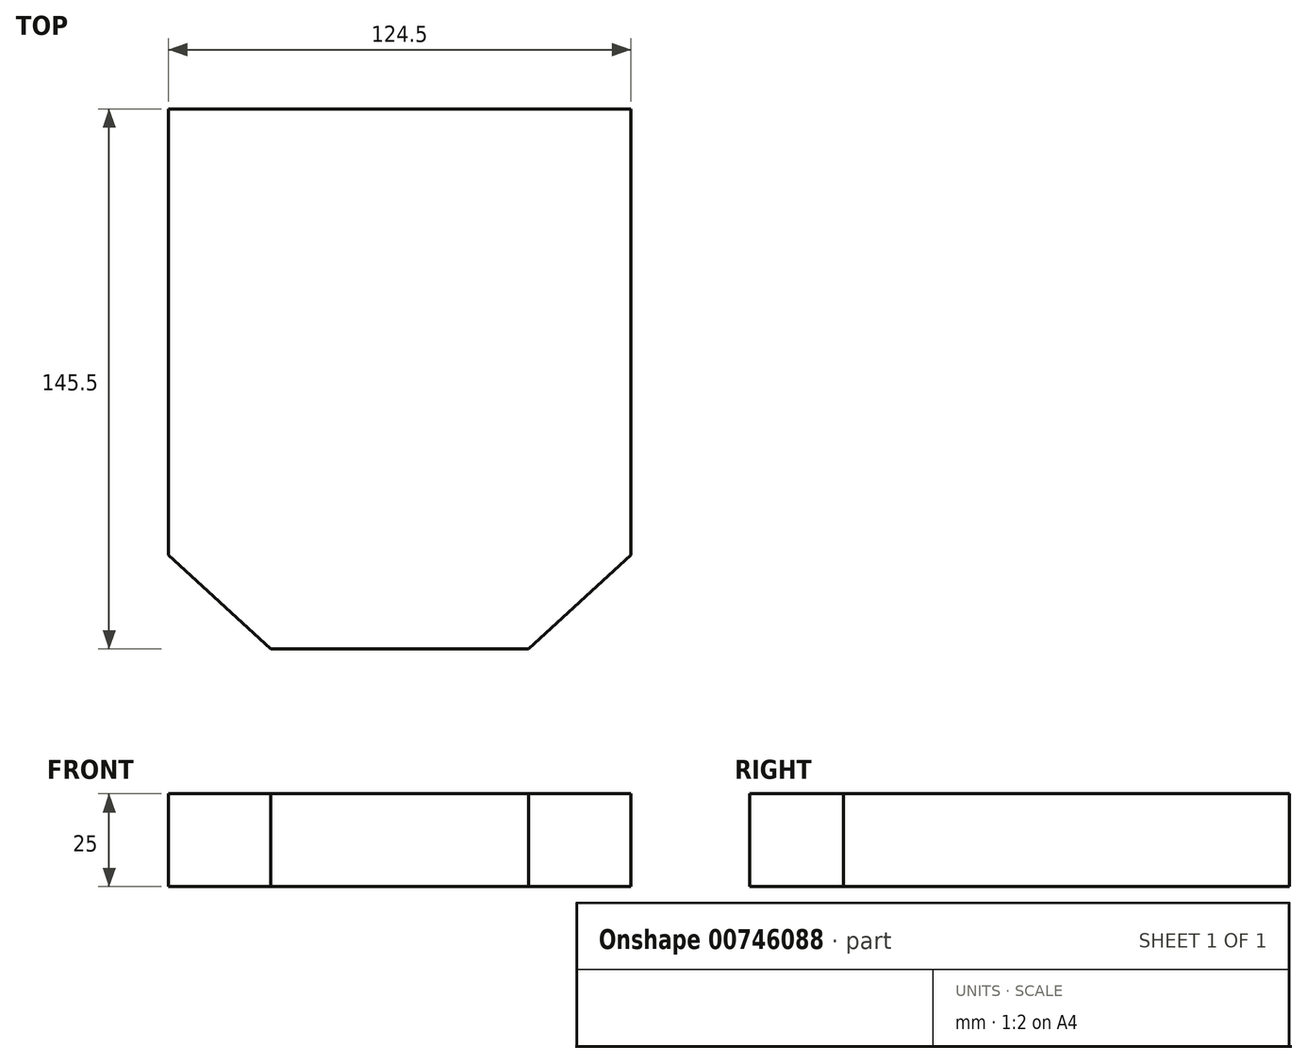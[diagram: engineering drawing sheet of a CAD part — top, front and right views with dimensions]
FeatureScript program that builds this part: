
annotation { "Feature Type Name" : "Feature", "Feature Type Description" : "" }
export const myFeature = defineFeature(function(context is Context, id is Id, definition is map)
    precondition{}
    {
        {
            var Q0;
            Q0=qCreatedBy(makeId("Top.planeOp"),FACE);
            var sketch = newSketch(context, id + "F0", { "sketchPlane" : qUnion([Q0])});
            skLineSegment(sketch, "E0.bottom", {"start": v(-55.19, 58.1) * mm, "end": v(59.31, 58.1) * mm});
            skLineSegment(sketch, "E0.top", {"start": v(-30.69, -77.4) * mm, "end": v(34.81, -77.4) * mm});
            skLineSegment(sketch, "E0.left", {"start": v(-55.19, 58.1) * mm, "end": v(-55.19, -54.9) * mm});
            skLineSegment(sketch, "E0.right", {"start": v(59.31, 58.1) * mm, "end": v(59.31, -54.9) * mm});
            skLineSegment(sketch, "E1", {"start": v(-55.19, -54.9) * mm, "end": v(-30.69, -77.4) * mm});
            skLineSegment(sketch, "E2", {"start": v(34.81, -77.4) * mm, "end": v(59.31, -54.9) * mm});
            skPoint(sketch, "E3.orphan", {"position": v(-55.19, -77.4) * mm});
            skPoint(sketch, "E4.orphan", {"position": v(59.31, -77.4) * mm});
            skSolve(sketch);
        }
        {
            var Q0;
            Q0=qCreatedBy(makeId("Top.planeOp"),FACE);
            var sketch = newSketch(context, id + "F1", { "sketchPlane" : qUnion([Q0])});
            skLineSegment(sketch, "E5.0", {"start": v(-60.19, -57.1) * mm, "end": v(-32.64, -82.4) * mm});
            skLineSegment(sketch, "E5.1", {"start": v(36.76, -82.4) * mm, "end": v(64.31, -57.1) * mm});
            skLineSegment(sketch, "E5.2", {"start": v(64.31, -57.1) * mm, "end": v(64.31, 63.1) * mm});
            skLineSegment(sketch, "E5.3", {"start": v(-32.64, -82.4) * mm, "end": v(36.76, -82.4) * mm});
            skLineSegment(sketch, "E5.4", {"start": v(64.31, 63.1) * mm, "end": v(-60.19, 63.1) * mm});
            skLineSegment(sketch, "E5.5", {"start": v(-60.19, 63.1) * mm, "end": v(-60.19, -57.1) * mm});
            skSolve(sketch);
        }
        {
            var Q0;
            Q0=makeQuery(id+"F1.imprint","IMPRINT",FACE,{"disambiguationData":[TD([[makeQuery(id+"F1.imprint","IMPRINT",EDGE,{"derivedFrom":sQuery(id+"F1.wireOp",EDGE,"E5.0")}),1.0]])]});
            extrude(context, id + "F2", {"entities" : qUnion([Q0]), "depth" : 25 * mm, "offsetDistance" : 25 * mm});
        }
    });
